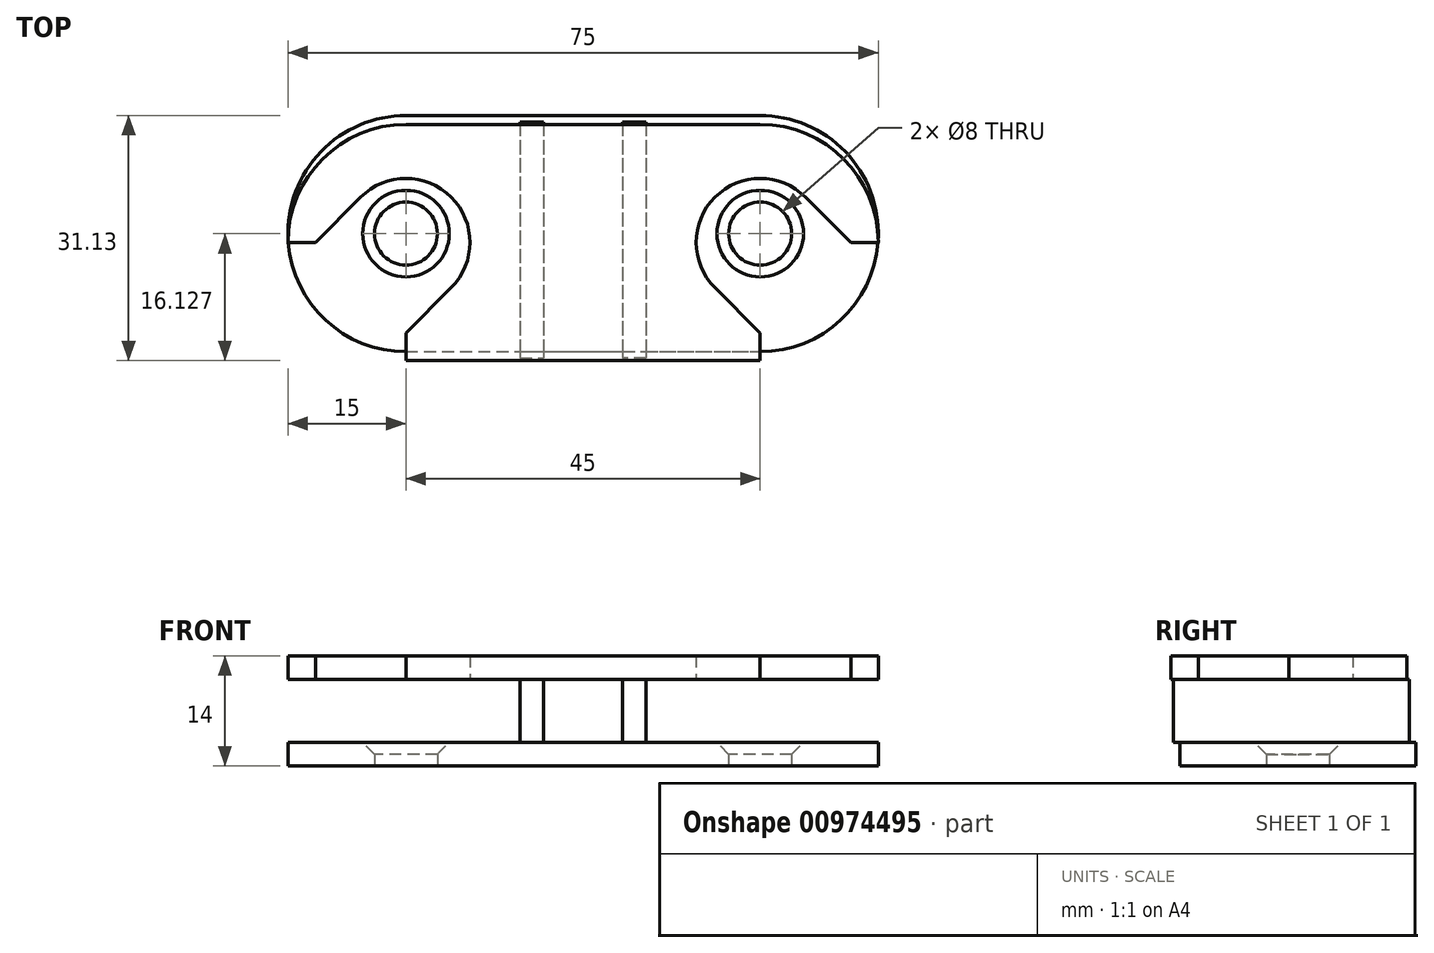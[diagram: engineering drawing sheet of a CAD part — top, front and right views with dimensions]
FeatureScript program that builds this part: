
annotation { "Feature Type Name" : "Feature", "Feature Type Description" : "" }
export const myFeature = defineFeature(function(context is Context, id is Id, definition is map)
    precondition{}
    {
        {
            var Q0;
            Q0=qCreatedBy(makeId("Top.planeOp"),FACE);
            var sketch = newSketch(context, id + "F0", { "sketchPlane" : qUnion([Q0])});
            skArc(sketch, "E0", {"start": v(-22.5, 15) * mm, "mid": v(-33.1, 10.6) * mm, "end": v(-37.5, 0) * mm});
            skArc(sketch, "E1", {"start": v(37.5, 0) * mm, "mid": v(33.1, 10.6) * mm, "end": v(22.5, 15) * mm});
            skLineSegment(sketch, "E2", {"start": v(-22.5, 15) * mm, "end": v(22.5, 15) * mm});
            skLineSegment(sketch, "E3", {"start": v(-22.5, -15) * mm, "end": v(22.5, -15) * mm});
            skLineSegment(sketch, "E4", {"start": v(-37.5, 0) * mm, "end": v(-34, 0) * mm});
            skLineSegment(sketch, "E5", {"start": v(-22.5, -15) * mm, "end": v(-22.5, -11.5) * mm});
            skLineSegment(sketch, "E6", {"start": v(-34, 0) * mm, "end": v(-28.25, 5.75) * mm});
            skLineSegment(sketch, "E7", {"start": v(-22.5, -11.5) * mm, "end": v(-16.75, -5.75) * mm});
            skArc(sketch, "E8", {"start": v(-16.75, -5.75) * mm, "mid": v(-16.75, 5.75) * mm, "end": v(-28.25, 5.75) * mm});
            skLineSegment(sketch, "E9.MirrorCS", {"start": v(37.5, 0) * mm, "end": v(34, 0) * mm});
            skLineSegment(sketch, "E10.MirrorCS", {"start": v(34, 0) * mm, "end": v(28.25, 5.75) * mm});
            skArc(sketch, "E11.MirrorCS", {"start": v(16.75, -5.75) * mm, "mid": v(16.75, 5.75) * mm, "end": v(28.25, 5.75) * mm});
            skLineSegment(sketch, "E12.MirrorCS", {"start": v(22.5, -11.5) * mm, "end": v(16.75, -5.75) * mm});
            skLineSegment(sketch, "E13.MirrorCS", {"start": v(22.5, -15) * mm, "end": v(22.5, -11.5) * mm});
            skSolve(sketch);
        }
        {
            var Q0;
            Q0 = qSketchRegion(id + "F0", true);
            extrude(context, id + "F1", {"entities" : qUnion([Q0]), "depth" : 3 * mm, "offsetDistance" : 25 * mm});
        }
        {
            var Q0;
            Q0=qCreatedBy(makeId("Top.planeOp"),FACE);
            cPlane(context, id + "F2", {"entities" : qUnion([Q0]), "cplaneType" : CPlaneType.OFFSET, "offset" : 11 * mm, "oppositeDirection" : true, "width" : 150 * mm, "height" : 150 * mm});
        }
        {
            var Q0;
            Q0=qCreatedBy(id+"F2.planeOp",FACE);
            var sketch = newSketch(context, id + "F3", { "sketchPlane" : qUnion([Q0])});
            skArc(sketch, "E14", {"start": v(-22.5, 15.83) * mm, "mid": v(-33.1, 11.43) * mm, "end": v(-37.5, 0.83) * mm});
            skArc(sketch, "E15", {"start": v(37.5, 0.83) * mm, "mid": v(33.1, 11.43) * mm, "end": v(22.5, 15.83) * mm});
            skLineSegment(sketch, "E16", {"start": v(-22.5, 15.83) * mm, "end": v(22.5, 15.83) * mm});
            skLineSegment(sketch, "E17", {"start": v(-22.5, -14.17) * mm, "end": v(22.5, -14.17) * mm});
            skArc(sketch, "E18", {"start": v(22.5, -14.17) * mm, "mid": v(37.5, 0.83) * mm, "end": v(22.5, 15.83) * mm});
            skArc(sketch, "E19", {"start": v(-22.5, 15.83) * mm, "mid": v(-37.5, 0.83) * mm, "end": v(-22.5, -14.17) * mm});
            skCircle(sketch, "E20", {"center": v(-22.5, 0.83) * mm, "radius": 4 * mm});
            skCircle(sketch, "E21", {"center": v(22.5, 0.83) * mm, "radius": 4 * mm});
            skSolve(sketch);
        }
        {
            var Q0;
            Q0=makeQuery(id+"F1.opExtrude","SWEPT_BODY",BODY,{"disambiguationData":[OSD([sQuery(id+"F0.wireOp",EDGE,"E0"),sQuery(id+"F0.wireOp",EDGE,"E1"),sQuery(id+"F0.wireOp",EDGE,"E2"),sQuery(id+"F0.wireOp",EDGE,"E3"),sQuery(id+"F0.wireOp",EDGE,"E4"),sQuery(id+"F0.wireOp",EDGE,"E5"),sQuery(id+"F0.wireOp",EDGE,"E6"),sQuery(id+"F0.wireOp",EDGE,"E7"),sQuery(id+"F0.wireOp",EDGE,"E8"),sQuery(id+"F0.wireOp",EDGE,"E9.MirrorCS"),sQuery(id+"F0.wireOp",EDGE,"E10.MirrorCS"),sQuery(id+"F0.wireOp",EDGE,"E11.MirrorCS"),sQuery(id+"F0.wireOp",EDGE,"E12.MirrorCS"),sQuery(id+"F0.wireOp",EDGE,"E13.MirrorCS")])]});
            var Q1;
            Q1=sQuery(id+"F3.wireOp",EDGE,"E16");
            transform(context, id + "F4", {"entities" : qUnion([Q0]), "transformType" : TransformType.TRANSLATION_3D, "dx" : 0 * mm, "dy" : -0.3 * mm, "dz" : 0 * mm, "makeCopy" : false});
        }
        {
            var Q0;
            Q0 = qSketchRegion(id + "F3", true);
            extrude(context, id + "F5", {"entities" : qUnion([Q0]), "depth" : 3 * mm, "offsetDistance" : 25 * mm});
        }
        {
            var Q0;
            Q0=makeQuery(id+"F5.opExtrude","CAP_EDGE",EDGE,{"disambiguationData":[OSD([sQuery(id+"F3.wireOp",EDGE,"E20")])],"isStart":false});
            var Q1;
            Q1=makeQuery(id+"F5.opExtrude","CAP_EDGE",EDGE,{"disambiguationData":[OSD([sQuery(id+"F3.wireOp",EDGE,"E21")])],"isStart":false});
            chamfer(context, id + "F6", {"entities" : qUnion([Q0, Q1]), "width" : 1.5 * mm, "tangentPropagation" : true});
        }
        {
            var Q0;
            Q0=qCreatedBy(makeId("Top.planeOp"),FACE);
            cPlane(context, id + "F7", {"entities" : qUnion([Q0]), "cplaneType" : CPlaneType.OFFSET, "offset" : 8 * mm, "oppositeDirection" : true, "width" : 150 * mm, "height" : 150 * mm});
        }
        {
            var Q0;
            Q0=qCreatedBy(id+"F7.planeOp",FACE);
            var sketch = newSketch(context, id + "F8", { "sketchPlane" : qUnion([Q0])});
            skLineSegment(sketch, "E22.bottom", {"start": v(-8, 15) * mm, "end": v(-5, 15) * mm});
            skLineSegment(sketch, "E22.top", {"start": v(-8, -15) * mm, "end": v(-5, -15) * mm});
            skLineSegment(sketch, "E22.left", {"start": v(-8, 15) * mm, "end": v(-8, -15) * mm});
            skLineSegment(sketch, "E22.right", {"start": v(-5, 15) * mm, "end": v(-5, -15) * mm});
            skPoint(sketch, "E22.middle", {"position": v(-6.5, 0) * mm});
            skLineSegment(sketch, "E23.MirrorCS", {"start": v(5, 15) * mm, "end": v(5, -15) * mm});
            skLineSegment(sketch, "E24.MirrorCS", {"start": v(8, 15) * mm, "end": v(5, 15) * mm});
            skLineSegment(sketch, "E25.MirrorCS", {"start": v(8, 15) * mm, "end": v(8, -15) * mm});
            skLineSegment(sketch, "E26.MirrorCS", {"start": v(8, -15) * mm, "end": v(5, -15) * mm});
            skSolve(sketch);
        }
        {
            var Q0;
            Q0 = qSketchRegion(id + "F8", true);
            extrude(context, id + "F9", {"entities" : qUnion([Q0]), "operationType" : NewBodyOperationType.ADD, "depth" : 8 * mm, "offsetDistance" : 25 * mm});
        }
    });
